# Revit family: REFLECTOR LANDSCAPE 01_RM16W.2.12
name_source: partatom
category: Luminarias
units: mm (PartAtom-declared; Revit-internal decimal feet)

## family parameters
Compartido = No
Corte con vacíos al cargar = No
Cota de conector redondo = Diámetro de uso
Origen de luz = Sí
Punto de cálculo de habitación = No
Se basa en plano de trabajo = Sí
Siempre vertical = No
Tipo de pieza = Normal

## types (1)
- RM16W.2.12
    Archivo de red fotométrica = RM16W.2_12º.ies
    Cambio de temperatura de color de luz atenuada = Curva de lámpara incandescente
    Comentarios de vataje = 100-277V
    Descripción = LUMINARIA TIPO REFLECTOR MONOCROMATICO DIRIGIBLE, CUERPO EN ALUMINIO FUNDIDO A PRESION CUBIERTO DE POLVO GRIS OSCURO Y VIDRIO TEMPLADO DE 3MM, CON UN PESO DE 2KG, CON 130MM DE LARGO POR 170MM DE ALTURA POR 110MM DE DIAMETRO, CUENTA CON 1 LED TIPO NICHIA CON UN CONSUMO DE 17W, 1225 LUMENES, IP 66, IRC 80, IK06, CABLE H05RN DE 0.5M, APERTURA DE 12 GRADOS POR PROYECTO, ALIMENTADA A 100-277V. ACCESORIOS OPCIONALES.
    Elevación por defecto = 0 mm  [stored 0 ft]
    Fabricante = BRILLANT
    Filtro de color = 16777215
    Lámpara = NICHIA
    Modelo = RM16W.2.12
    Watt per fixture = 17
    Ángulo de inclinación = 32.00°

note: [stored X ft] marks values corroborated as IEEE doubles in the binary element streams (Revit-internal decimal feet)

## geometry (parser evidence)
native form markers: Blend x2
no freeform markers — native parametric forms only
